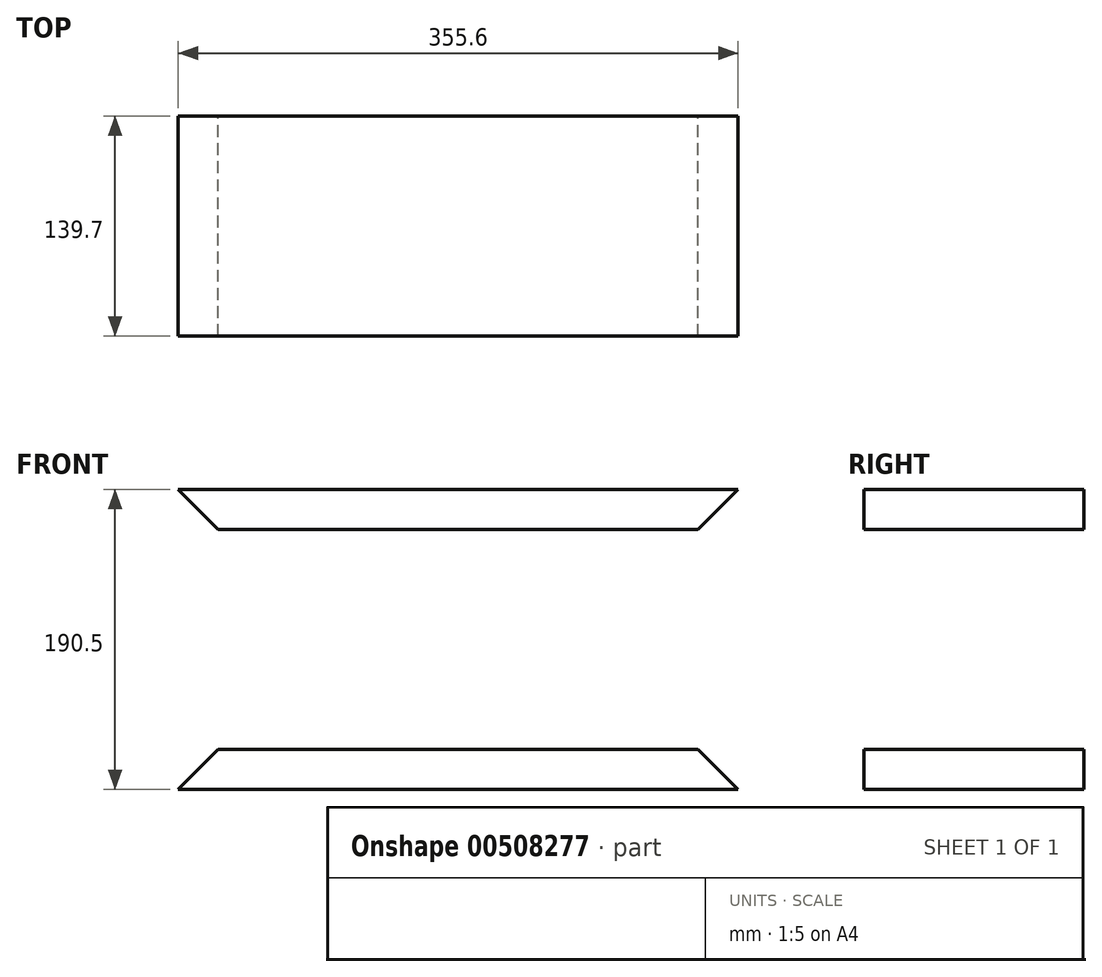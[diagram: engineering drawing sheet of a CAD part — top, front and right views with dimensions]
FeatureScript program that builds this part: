
annotation { "Feature Type Name" : "Feature", "Feature Type Description" : "" }
export const myFeature = defineFeature(function(context is Context, id is Id, definition is map)
    precondition{}
    {
        {
            var Q0;
            Q0=qCreatedBy(makeId("Front.planeOp"),FACE);
            var sketch = newSketch(context, id + "F0", { "sketchPlane" : qUnion([Q0])});
            skLineSegment(sketch, "E0.bottom", {"start": v(-310.5, -10.15) * mm, "end": v(-5.7, -10.15) * mm});
            skLineSegment(sketch, "E0.top", {"start": v(-335.9, -35.55) * mm, "end": v(19.7, -35.55) * mm});
            skLineSegment(sketch, "E0.left", {"start": v(-310.5, -10.15) * mm, "end": v(-335.9, -35.55) * mm});
            skLineSegment(sketch, "E0.right", {"start": v(-5.7, -10.15) * mm, "end": v(19.7, -35.55) * mm});
            skLineSegment(sketch, "E1.bottom", {"start": v(-335.9, -35.55) * mm, "end": v(-310.5, -10.15) * mm});
            skLineSegment(sketch, "E1.top", {"start": v(-335.9, 154.95) * mm, "end": v(-310.5, 129.55) * mm});
            skLineSegment(sketch, "E1.left", {"start": v(-335.9, -35.55) * mm, "end": v(-335.9, 154.95) * mm});
            skLineSegment(sketch, "E1.right", {"start": v(-310.5, -10.15) * mm, "end": v(-310.5, 129.55) * mm});
            skLineSegment(sketch, "E2.bottom", {"start": v(19.7, -35.55) * mm, "end": v(-5.7, -10.15) * mm});
            skLineSegment(sketch, "E2.top", {"start": v(19.7, 154.95) * mm, "end": v(-5.7, 129.55) * mm});
            skLineSegment(sketch, "E2.left", {"start": v(19.7, -35.55) * mm, "end": v(19.7, 154.95) * mm});
            skLineSegment(sketch, "E2.right", {"start": v(-5.7, -10.15) * mm, "end": v(-5.7, 129.55) * mm});
            skLineSegment(sketch, "E3.left", {"start": v(-335.9, 154.95) * mm, "end": v(-335.9, 129.48) * mm});
            skLineSegment(sketch, "E3.right", {"start": v(19.7, 154.95) * mm, "end": v(19.7, 129.48) * mm});
            skLineSegment(sketch, "E4.bottom", {"start": v(-335.9, 154.95) * mm, "end": v(19.7, 154.95) * mm});
            skLineSegment(sketch, "E4.top", {"start": v(-310.5, 129.55) * mm, "end": v(-5.7, 129.55) * mm});
            skSolve(sketch);
        }
        {
            var Q0;
            Q0=makeQuery(id+"F0.imprint","IMPRINT",FACE,{"disambiguationData":[TD([[makeQuery(id+"F0.imprint","IMPRINT",EDGE,{"derivedFrom":sQuery(id+"F0.wireOp",EDGE,"E4.bottom")}),-1.0]])]});
            var Q1;
            Q1=makeQuery(id+"F0.imprint","IMPRINT",FACE,{"disambiguationData":[TD([[makeQuery(id+"F0.imprint","IMPRINT",EDGE,{"derivedFrom":sQuery(id+"F0.wireOp",EDGE,"E1.bottom")}),1.0]])]});
            var Q2;
            Q2=makeQuery(id+"F0.imprint","IMPRINT",FACE,{"disambiguationData":[TD([[makeQuery(id+"F0.imprint","IMPRINT",EDGE,{"derivedFrom":sQuery(id+"F0.wireOp",EDGE,"E0.bottom")}),-1.0]])]});
            var Q3;
            Q3=makeQuery(id+"F0.imprint","IMPRINT",FACE,{"disambiguationData":[TD([[makeQuery(id+"F0.imprint","IMPRINT",EDGE,{"derivedFrom":sQuery(id+"F0.wireOp",EDGE,"E2.bottom")}),-1.0]])]});
            extrude(context, id + "F1", {"entities" : qUnion([Q0, Q1, Q2, Q3]), "endBound" : BoundingType.SYMMETRIC, "depth" : 139.7 * mm});
        }
    });
